# Revit family: TAG3
name_source: partatom
category: Furniture
units: mm (PartAtom-declared; Revit-internal decimal feet)

## family parameters
Always vertical = Yes
Cut with Voids When Loaded = No
OmniClass Number = 23.40.20.00
OmniClass Title = General Furniture and Specialties
Room Calculation Point = No
Shared = No
Work Plane-Based = No

## types (1)
- Office1
    Cost = 40296 $
    Default Elevation = 0' - 0"
    Description = 6 x Natick Black Configurable Task Chair, 1 x Natick - Lumbar Support- Black, 3 x Duplex Outlet - Line 1 - Black, 3 x Duplex Outlet - Line 2 - Black, 3 x Duplex Outlet - Line 3 - Black, 3 x Duplex Outlet - Line 4 Dedicated - Black, 2 x 51 in. Electrical Jumper (Pt 30E), 2 x Oxygen Laminate Double Sided End Panel 28Hx48W, 2 x Unv. Spine Insert Screen - Glass .250 16H x 72W, 1 x Unv. Spine Insert Screen - Glass .250 16H x 72W, 1 x Base Infeed - with Pole - 8 Wire 4 Circuit - Side Mounted, 2 x Double Bench Powered w/Grommet 48D X 72W, 1 x Double Bench Powered w/Grommet 48D X 72W, 2 x Double Sided Shared Straight Leg Kit - 48D, 1 x Calibrate Single Wrap Dry Planter 50Hx48Wx18D, 4 x CBX Double Door Locker Left 42h x 12w x 18d
    Exported From CET Designer = Yes
    Manufacturer = AIS
    Model = 4900C
    Show Office1 = Yes
    VisibilityIndex = 0

## geometry (parser evidence)
native form markers: Sweep x3
no freeform markers — native parametric forms only
